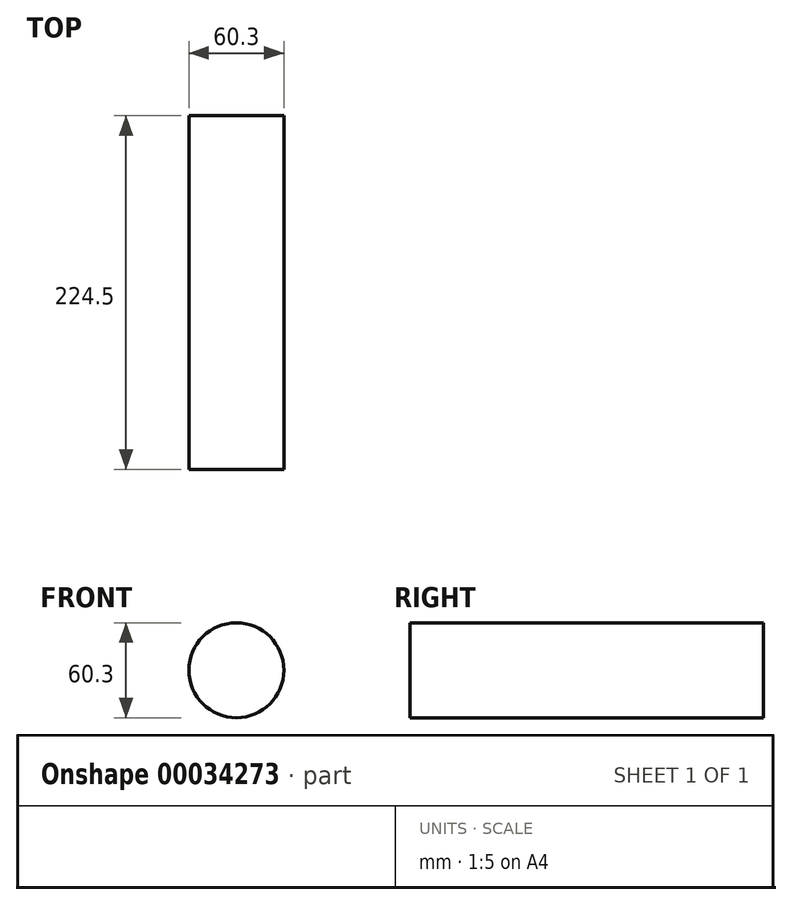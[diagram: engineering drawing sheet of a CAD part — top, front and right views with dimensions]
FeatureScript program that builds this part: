
annotation { "Feature Type Name" : "Feature", "Feature Type Description" : "" }
export const myFeature = defineFeature(function(context is Context, id is Id, definition is map)
    precondition{}
    {
        {
            var Q0;
            Q0=qCreatedBy(makeId("Front.planeOp"),FACE);
            var sketch = newSketch(context, id + "F0", { "sketchPlane" : qUnion([Q0])});
            skCircle(sketch, "E0", {"center": v(0, 0) * mm, "radius": 30.15 * mm});
            skSolve(sketch);
        }
        {
            var Q0;
            Q0=makeQuery(id+"F0.imprint","IMPRINT",FACE,{"disambiguationData":[TD([[makeQuery(id+"F0.imprint","IMPRINT",EDGE,{"derivedFrom":sQuery(id+"F0.wireOp",EDGE,"E0")}),1.0]])]});
            extrude(context, id + "F1", {"entities" : qUnion([Q0]), "depth" : 224.5 * mm});
        }
    });
